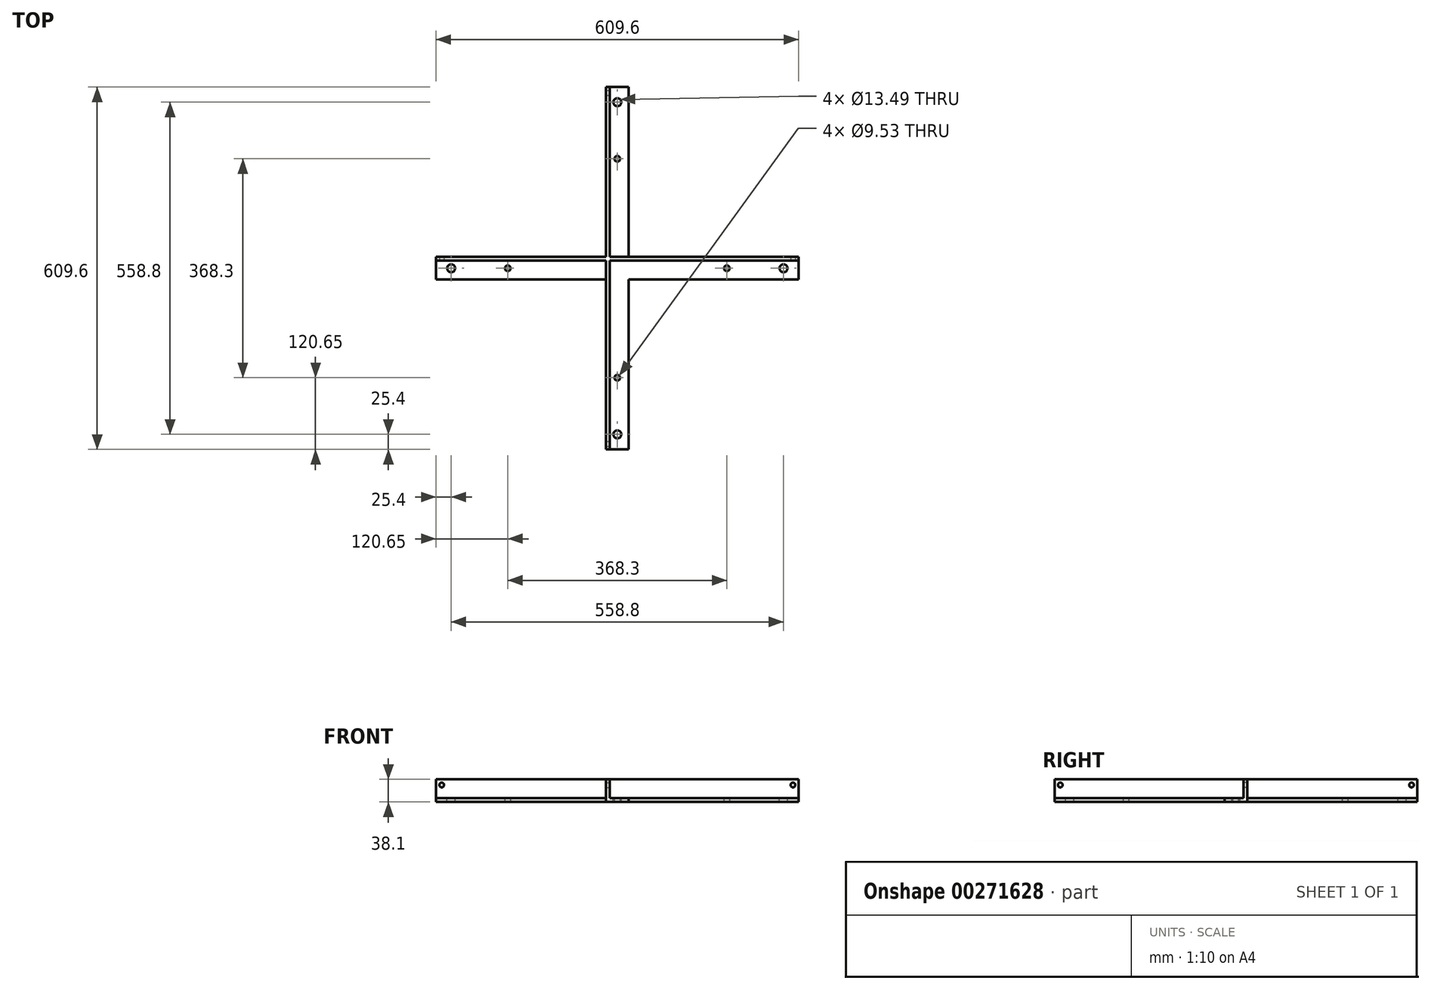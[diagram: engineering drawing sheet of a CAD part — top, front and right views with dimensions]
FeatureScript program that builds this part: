
annotation { "Feature Type Name" : "Feature", "Feature Type Description" : "" }
export const myFeature = defineFeature(function(context is Context, id is Id, definition is map)
    precondition{}
    {
        {
            var Q0;
            Q0=qCreatedBy(makeId("Front.planeOp"),FACE);
            var sketch = newSketch(context, id + "F0", { "sketchPlane" : qUnion([Q0])});
            skLineSegment(sketch, "E0", {"start": v(-19.05, 38.1) * mm, "end": v(-19.05, 0) * mm});
            skLineSegment(sketch, "E1", {"start": v(-19.05, 0) * mm, "end": v(19.05, 0) * mm});
            skLineSegment(sketch, "E2.0", {"start": v(-12.7, 6.35) * mm, "end": v(19.05, 6.35) * mm});
            skLineSegment(sketch, "E2.1", {"start": v(-12.7, 38.1) * mm, "end": v(-12.7, 6.35) * mm});
            skLineSegment(sketch, "E3", {"start": v(-19.05, 38.1) * mm, "end": v(-12.7, 38.1) * mm});
            skLineSegment(sketch, "E4", {"start": v(19.05, 6.35) * mm, "end": v(19.05, 0) * mm});
            skSolve(sketch);
        }
        {
            var Q0;
            Q0 = qSketchRegion(id + "F0", true);
            extrude(context, id + "F1", {"entities" : qUnion([Q0]), "endBound" : BoundingType.SYMMETRIC, "oppositeDirection" : true, "depth" : 609.6 * mm});
        }
        {
            var Q0;
            Q0 = qSketchRegion(id + "F0", true);
            extrude(context, id + "F2", {"entities" : qUnion([Q0]), "operationType" : NewBodyOperationType.ADD, "endBound" : BoundingType.SYMMETRIC, "depth" : 609.6 * mm});
        }
        {
            var Q0;
            Q0=qCreatedBy(makeId("Right.planeOp"),FACE);
            var sketch = newSketch(context, id + "F3", { "sketchPlane" : qUnion([Q0])});
            skLineSegment(sketch, "E5", {"start": v(-19.05, 0) * mm, "end": v(19.05, 0) * mm});
            skLineSegment(sketch, "E6", {"start": v(19.05, 0) * mm, "end": v(19.05, 38.1) * mm});
            skLineSegment(sketch, "E7.0", {"start": v(12.7, 6.35) * mm, "end": v(12.7, 38.1) * mm});
            skLineSegment(sketch, "E7.1", {"start": v(-19.05, 6.35) * mm, "end": v(12.7, 6.35) * mm});
            skLineSegment(sketch, "E8", {"start": v(12.7, 38.1) * mm, "end": v(19.05, 38.1) * mm});
            skLineSegment(sketch, "E9", {"start": v(-19.05, 6.35) * mm, "end": v(-19.05, 0) * mm});
            skSolve(sketch);
        }
        {
            var Q0;
            Q0 = qSketchRegion(id + "F3", true);
            extrude(context, id + "F4", {"entities" : qUnion([Q0]), "operationType" : NewBodyOperationType.ADD, "endBound" : BoundingType.SYMMETRIC, "depth" : 609.6 * mm});
        }
        {
            var Q0;
            Q0=makeQuery(id+"F4.boolean.opBoolean","SPLIT",FACE,{"derivedFrom":makeQuery(id+"F1.opExtrude","SWEPT_FACE",FACE,{"disambiguationData":[OSD([sQuery(id+"F0.wireOp",EDGE,"E2.0")])]})});
            var sketch = newSketch(context, id + "F5", { "sketchPlane" : qUnion([Q0])});
            skCircle(sketch, "E10", {"center": v(0, 279.4) * mm, "radius": 6.74 * mm});
            skCircle(sketch, "E11", {"center": v(279.4, 0) * mm, "radius": 6.74 * mm});
            skCircle(sketch, "E12", {"center": v(-279.4, 0) * mm, "radius": 6.74 * mm});
            skCircle(sketch, "E13", {"center": v(0, -279.4) * mm, "radius": 6.74 * mm});
            skLineSegment(sketch, "E14", {"start": v(0, 0) * mm, "end": v(96.1, 0) * mm, "construction": true});
            skLineSegment(sketch, "E15", {"start": v(0, 0) * mm, "end": v(0, -78.39) * mm, "construction": true});
            skSolve(sketch);
        }
        {
            var Q0;
            Q0=makeQuery(id+"F5.imprint","IMPRINT",FACE,{"disambiguationData":[TD([[makeQuery(id+"F5.imprint","IMPRINT",EDGE,{"derivedFrom":sQuery(id+"F5.wireOp",EDGE,"E12")}),1.0]])]});
            var Q1;
            Q1=makeQuery(id+"F5.imprint","IMPRINT",FACE,{"disambiguationData":[TD([[makeQuery(id+"F5.imprint","IMPRINT",EDGE,{"derivedFrom":sQuery(id+"F5.wireOp",EDGE,"E13")}),1.0]])]});
            var Q2;
            Q2=makeQuery(id+"F5.imprint","IMPRINT",FACE,{"disambiguationData":[TD([[makeQuery(id+"F5.imprint","IMPRINT",EDGE,{"derivedFrom":sQuery(id+"F5.wireOp",EDGE,"E10")}),1.0]])]});
            var Q3;
            Q3=makeQuery(id+"F5.imprint","IMPRINT",FACE,{"disambiguationData":[TD([[makeQuery(id+"F5.imprint","IMPRINT",EDGE,{"derivedFrom":sQuery(id+"F5.wireOp",EDGE,"E11")}),1.0]])]});
            extrude(context, id + "F6", {"entities" : qUnion([Q0, Q1, Q2, Q3]), "operationType" : NewBodyOperationType.REMOVE, "endBound" : BoundingType.THROUGH_ALL, "oppositeDirection" : true, "depth" : 25.4 * mm});
        }
        {
            var Q0;
            {var subQ2=sQuery(id+"F3.wireOp",EDGE,"E7.0");Q0=makeQuery(id+"F4.boolean.opBoolean","SPLIT",FACE,{"disambiguationData":[TD([makeQuery(id+"F1.opExtrude","SWEPT_FACE",FACE,{"disambiguationData":[OSD([sQuery(id+"F0.wireOp",EDGE,"E2.0")])]})])],"derivedFrom":makeQuery(id+"F4.opExtrude","SWEPT_FACE",FACE,{"disambiguationData":[OSD([subQ2])]})});}
            var sketch = newSketch(context, id + "F7", { "sketchPlane" : qUnion([Q0])});
            skCircle(sketch, "E16", {"center": v(295.28, 28.58) * mm, "radius": 3.98 * mm});
            skCircle(sketch, "E17", {"center": v(-295.28, 28.58) * mm, "radius": 3.98 * mm});
            skSolve(sketch);
        }
        {
            var Q0;
            Q0 = qSketchRegion(id + "F7", true);
            extrude(context, id + "F8", {"entities" : qUnion([Q0]), "operationType" : NewBodyOperationType.REMOVE, "endBound" : BoundingType.THROUGH_ALL, "oppositeDirection" : true, "depth" : 25.4 * mm});
        }
        {
            var Q0;
            {var subQ2=sQuery(id+"F0.wireOp",EDGE,"E2.1");Q0=makeQuery(id+"F4.boolean.opBoolean","SPLIT",FACE,{"disambiguationData":[TD([makeQuery(id+"F4.opExtrude","SWEPT_FACE",FACE,{"disambiguationData":[OSD([sQuery(id+"F3.wireOp",EDGE,"E6")])]})])],"derivedFrom":makeQuery(id+"F1.opExtrude","SWEPT_FACE",FACE,{"disambiguationData":[OSD([subQ2])]})});}
            var sketch = newSketch(context, id + "F9", { "sketchPlane" : qUnion([Q0])});
            skCircle(sketch, "E18", {"center": v(295.28, 28.57) * mm, "radius": 3.98 * mm});
            skCircle(sketch, "E19", {"center": v(-295.28, 28.57) * mm, "radius": 3.98 * mm});
            skSolve(sketch);
        }
        {
            var Q0;
            Q0 = qSketchRegion(id + "F9", true);
            extrude(context, id + "F10", {"entities" : qUnion([Q0]), "operationType" : NewBodyOperationType.REMOVE, "endBound" : BoundingType.THROUGH_ALL, "oppositeDirection" : true, "depth" : 25.4 * mm});
        }
        {
            var Q0;
            Q0=makeQuery(id+"F4.boolean.opBoolean","SPLIT",FACE,{"derivedFrom":makeQuery(id+"F1.opExtrude","SWEPT_FACE",FACE,{"disambiguationData":[OSD([sQuery(id+"F0.wireOp",EDGE,"E2.0")])]})});
            var sketch = newSketch(context, id + "F11", { "sketchPlane" : qUnion([Q0])});
            skCircle(sketch, "E20", {"center": v(0, 184.15) * mm, "radius": 4.76 * mm});
            skCircle(sketch, "E21.1.0", {"center": v(-184.15, 0) * mm, "radius": 4.76 * mm});
            skCircle(sketch, "E21.2.0", {"center": v(0, -184.15) * mm, "radius": 4.76 * mm});
            skCircle(sketch, "E21.3.0", {"center": v(184.15, 0) * mm, "radius": 4.76 * mm});
            skPoint(sketch, "E21.center", {"position": v(0, 0) * mm});
            skSolve(sketch);
        }
        {
            var Q0;
            Q0=makeQuery(id+"F11.imprint","IMPRINT",FACE,{"disambiguationData":[TD([[makeQuery(id+"F11.imprint","IMPRINT",EDGE,{"derivedFrom":sQuery(id+"F11.wireOp",EDGE,"E20")}),1.0]])]});
            var Q1;
            Q1=makeQuery(id+"F11.imprint","IMPRINT",FACE,{"disambiguationData":[TD([[makeQuery(id+"F11.imprint","IMPRINT",EDGE,{"derivedFrom":sQuery(id+"F11.wireOp",EDGE,"E21.3.0")}),1.0]])]});
            var Q2;
            Q2=makeQuery(id+"F11.imprint","IMPRINT",FACE,{"disambiguationData":[TD([[makeQuery(id+"F11.imprint","IMPRINT",EDGE,{"derivedFrom":sQuery(id+"F11.wireOp",EDGE,"E21.2.0")}),1.0]])]});
            var Q3;
            Q3=makeQuery(id+"F11.imprint","IMPRINT",FACE,{"disambiguationData":[TD([[makeQuery(id+"F11.imprint","IMPRINT",EDGE,{"derivedFrom":sQuery(id+"F11.wireOp",EDGE,"E21.1.0")}),1.0]])]});
            extrude(context, id + "F12", {"entities" : qUnion([Q0, Q1, Q2, Q3]), "operationType" : NewBodyOperationType.REMOVE, "endBound" : BoundingType.THROUGH_ALL, "oppositeDirection" : true, "depth" : 25.4 * mm});
        }
    });
